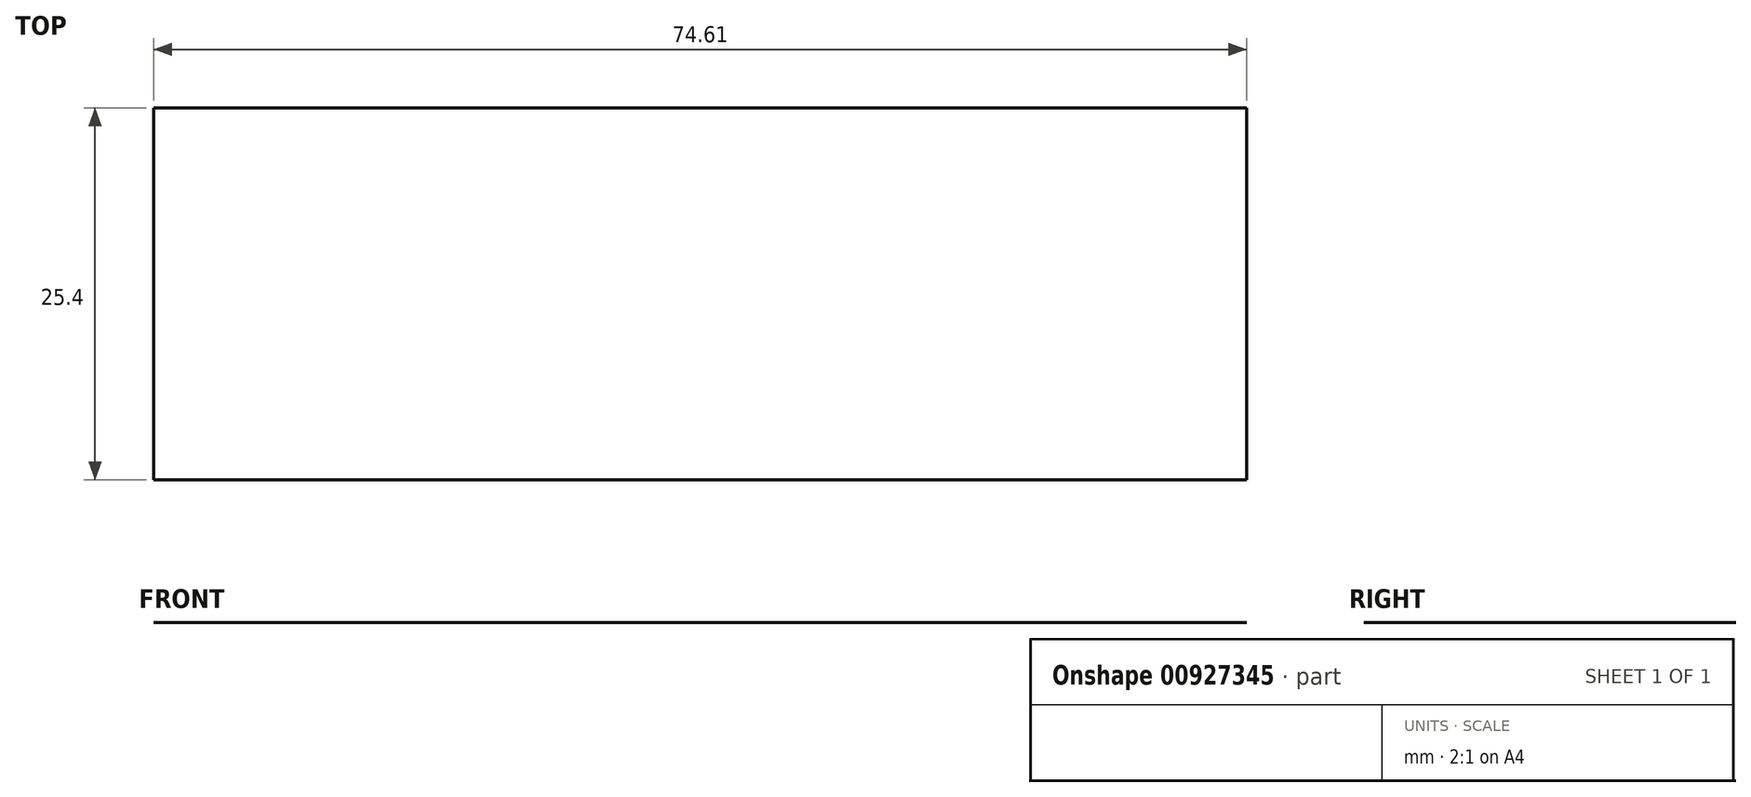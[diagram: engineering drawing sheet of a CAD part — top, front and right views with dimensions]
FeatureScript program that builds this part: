
annotation { "Feature Type Name" : "Feature", "Feature Type Description" : "" }
export const myFeature = defineFeature(function(context is Context, id is Id, definition is map)
    precondition{}
    {
        {
            var Q0;
            Q0=qCreatedBy(makeId("Front.planeOp"),FACE);
            var sketch = newSketch(context, id + "F0", { "sketchPlane" : qUnion([Q0])});
            skLineSegment(sketch, "E0.bottom", {"start": v(0, 0) * mm, "end": v(74.6, 0) * mm});
            skLineSegment(sketch, "E0.top", {"start": v(0, 36.81) * mm, "end": v(74.6, 36.81) * mm});
            skLineSegment(sketch, "E0.left", {"start": v(0, 0) * mm, "end": v(0, 36.81) * mm});
            skLineSegment(sketch, "E0.right", {"start": v(74.6, 0) * mm, "end": v(74.6, 36.81) * mm});
            skSolve(sketch);
        }
        {
            var Q0;
            Q0=sQuery(id+"F0.wireOp",EDGE,"E0.top");
            extrude(context, id + "F1", {"bodyType" : ToolBodyType.SURFACE, "surfaceEntities" : qUnion([Q0]), "depth" : 25.4 * mm, "offsetDistance" : 25.4 * mm});
        }
    });
